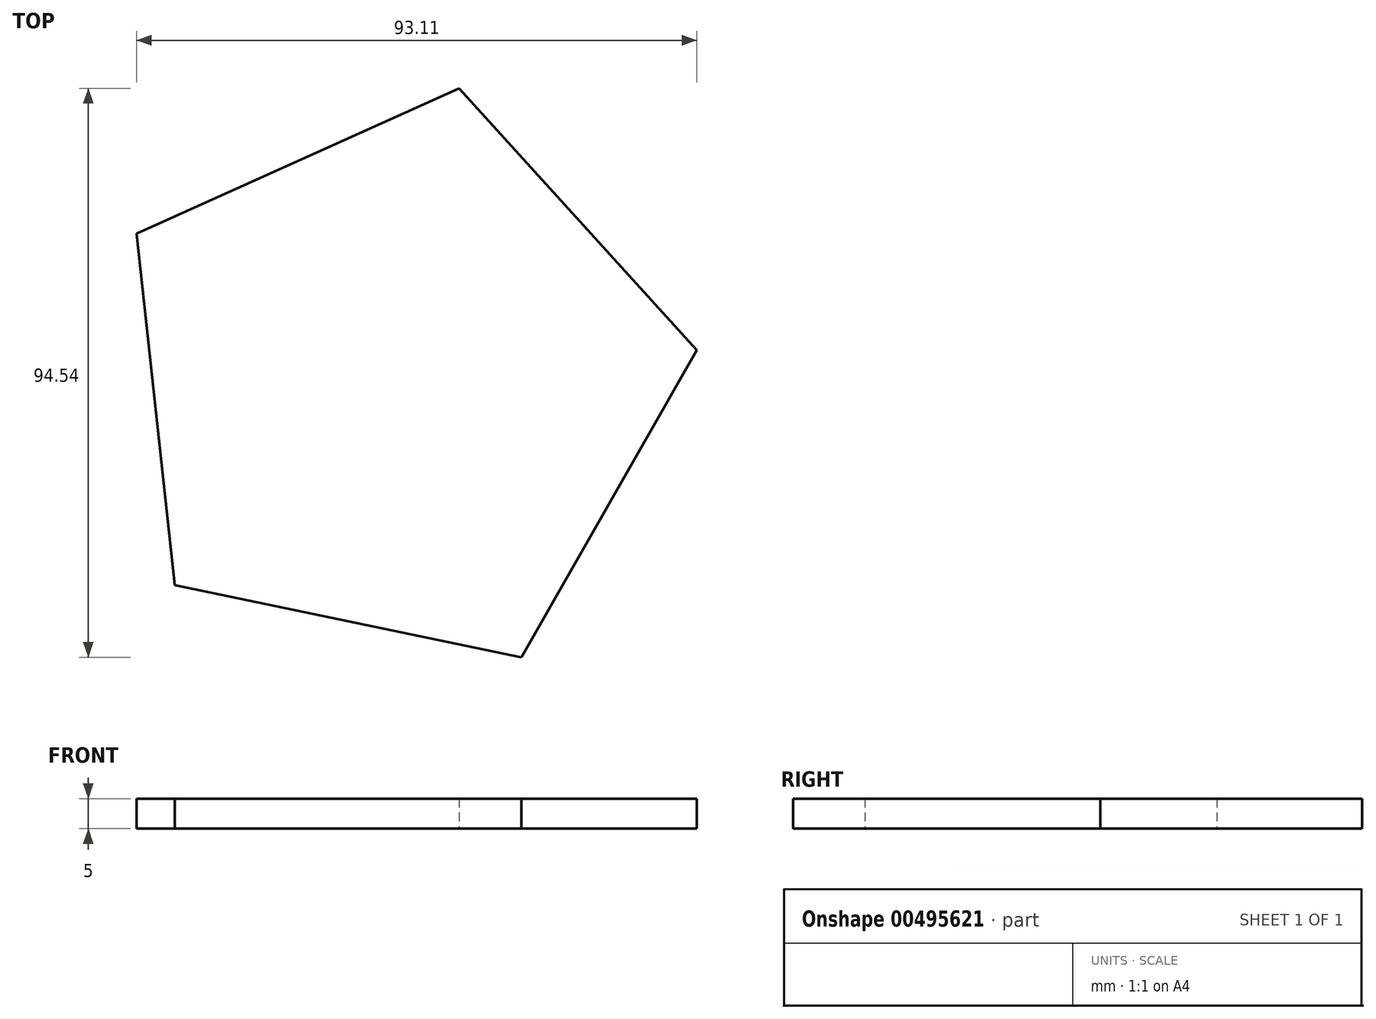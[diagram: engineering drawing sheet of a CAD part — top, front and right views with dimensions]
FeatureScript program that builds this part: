
annotation { "Feature Type Name" : "Feature", "Feature Type Description" : "" }
export const myFeature = defineFeature(function(context is Context, id is Id, definition is map)
    precondition{}
    {
        {
            var Q0;
            Q0=qCreatedBy(makeId("Top.planeOp"),FACE);
            var sketch = newSketch(context, id + "F0", { "sketchPlane" : qUnion([Q0])});
            skCircle(sketch, "E0.cCircle", {"center": v(-19.84, 20.07) * mm, "radius": 40.45 * mm, "construction": true});
            skLineSegment(sketch, "E0.0", {"start": v(29.86, 25.52) * mm, "end": v(0.7, -25.52) * mm});
            skLineSegment(sketch, "E0.1", {"start": v(0.7, -25.52) * mm, "end": v(-56.85, -13.55) * mm});
            skLineSegment(sketch, "E0.2", {"start": v(-56.85, -13.55) * mm, "end": v(-63.25, 44.88) * mm});
            skLineSegment(sketch, "E0.3", {"start": v(-63.25, 44.88) * mm, "end": v(-9.66, 69.02) * mm});
            skLineSegment(sketch, "E0.4", {"start": v(-9.66, 69.02) * mm, "end": v(29.86, 25.52) * mm});
            skPoint(sketch, "E0.0.midPoint", {"position": v(15.28, 0) * mm});
            skSolve(sketch);
        }
        {
            var Q0;
            Q0=makeQuery(id+"F0.imprint","IMPRINT",FACE,{"disambiguationData":[TD([[makeQuery(id+"F0.imprint","IMPRINT",EDGE,{"derivedFrom":sQuery(id+"F0.wireOp",EDGE,"E0.0")}),-1.0]])]});
            extrude(context, id + "F1", {"entities" : qUnion([Q0]), "depth" : 5 * mm});
        }
    });
